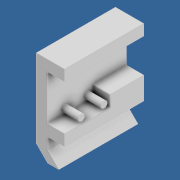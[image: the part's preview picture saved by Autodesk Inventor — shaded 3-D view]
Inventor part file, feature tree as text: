
AUTODESK INVENTOR PART (.ipt)
format: ipt  version: 2020 (Build 240168000, 168)  size: 164,352 bytes
history: native  units: mm
features: sketch x7, extrude x6, chamfer x2, split x1
ambient origin geometry x8: Origin, YZ Plane, XZ Plane, XY Plane, X Axis, Y Axis, Z Axis, Center Point
bodies: Solid1 (feature_tree)
feature tree (16):
  extrude  "Extrusion1"  Depth=56.0mm
  extrude  "Extrusion2"  Depth=40.0mm
  extrude  "Extrusion3"  Depth=7.8mm
  extrude  "Extrusion4"  Depth=4.6mm
  sketch  "Sketch14"  dims[d10=4.6mm d11=16.0mm]
  extrude  "Extrusion7"  Depth=16.0mm
  extrude  "Extrusion8"  Depth=12.0mm TaperAngle=0.0deg
  chamfer  "Chamfer1"  Distance=8.0mm
  chamfer  "Chamfer2"  Distance=26.0mm
  split  "Split1"
  sketch  "Sketch1"  dims[d0=39.6mm d1=56.0mm]
  sketch  "Sketch2"  dims[d2=40.0mm d3=0.0mm d4=24.4mm]
  sketch  "Sketch3"  dims[d5=31.8mm d6=7.8mm]
  sketch  "Sketch4"  dims[d7=64.0mm d8=0.0mm d9=4.6mm]
  sketch  "Sketch15"  dims[d12=12.0mm d13=26.0mm d14=0.0mm]
  sketch  "Sketch16"  dims[d15=24.0mm d16=8.0mm d17=26.0mm d18=0.0mm d35=24.0mm d36=0.0mm d37=24.0mm d38=8.0mm d39=8.0mm d40=8.0mm d41=8.0mm d42=8.0mm d43=16.0mm d44=0.0mm d45=0.0mm d46=8.0mm d47=2.0mm d48=45.0deg d49=8.0mm d50=2.0mm d51=45.0deg]
